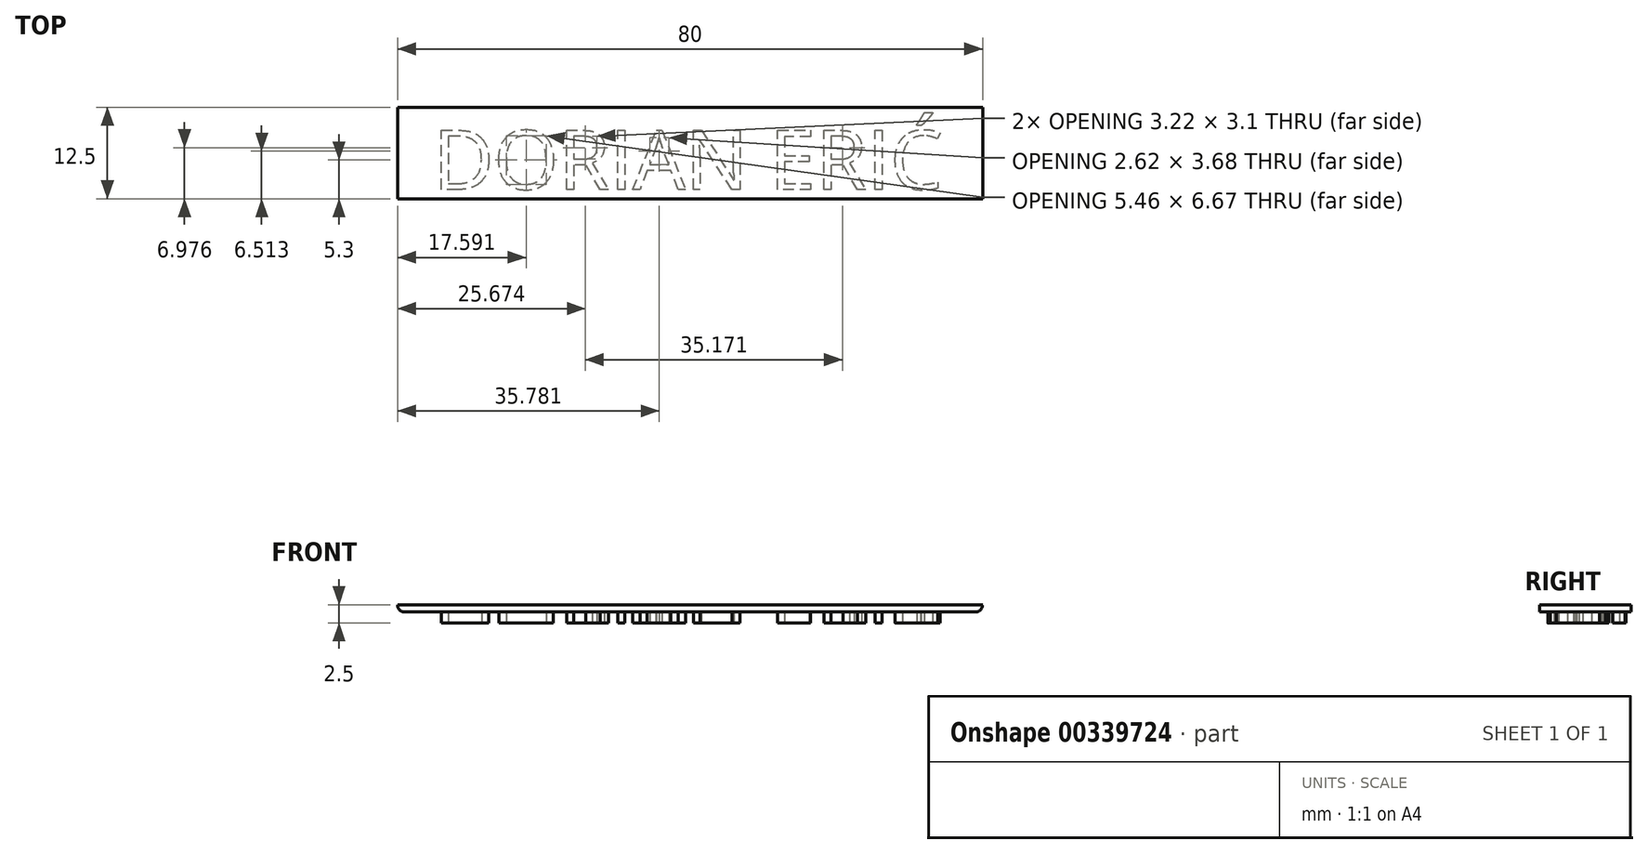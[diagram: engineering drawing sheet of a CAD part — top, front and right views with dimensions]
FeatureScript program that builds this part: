
annotation { "Feature Type Name" : "Feature", "Feature Type Description" : "" }
export const myFeature = defineFeature(function(context is Context, id is Id, definition is map)
    precondition{}
    {
        {
            var Q0;
            Q0=qCreatedBy(makeId("Top.planeOp"),FACE);
            var sketch = newSketch(context, id + "F0", { "sketchPlane" : qUnion([Q0])});
            skLineSegment(sketch, "E0.bottom", {"start": v(40, 6.25) * mm, "end": v(-40, 6.25) * mm});
            skLineSegment(sketch, "E0.top", {"start": v(40, -6.25) * mm, "end": v(-40, -6.25) * mm});
            skLineSegment(sketch, "E0.left", {"start": v(40, 6.25) * mm, "end": v(40, -6.25) * mm});
            skLineSegment(sketch, "E0.right", {"start": v(-40, 6.25) * mm, "end": v(-40, -6.25) * mm});
            skPoint(sketch, "E0.middle", {"position": v(0, 0) * mm});
            skText(sketch, "E1", { "text": "DORIAN ERIĆ", "fontName": "OpenSans-Regular.ttf"});
            const initialGuessF0  = {"E1": [-0.0351, -0.005, 1, 0, 0.00817]};
            skSetInitialGuess(sketch, initialGuessF0);
            skSolve(sketch);
        }
        {
            var Q0;
            Q0=makeQuery(id+"F0.imprint","IMPRINT",FACE,{"disambiguationData":[TD([[makeQuery(id+"F0.imprint","IMPRINT",EDGE,{"derivedFrom":sQuery(id+"F0.wireOp",EDGE,"E0.top")}),-1.0]])]});
            var sketch = newSketch(context, id + "F1", { "sketchPlane" : qUnion([Q0])});
            skLineSegment(sketch, "E2.bottom", {"start": v(40, -6.25) * mm, "end": v(-40, -6.25) * mm});
            skLineSegment(sketch, "E2.top", {"start": v(40, 6.25) * mm, "end": v(-40, 6.25) * mm});
            skLineSegment(sketch, "E2.left", {"start": v(40, -6.25) * mm, "end": v(40, 6.25) * mm});
            skLineSegment(sketch, "E2.right", {"start": v(-40, -6.25) * mm, "end": v(-40, 6.25) * mm});
            skPoint(sketch, "E2.middle", {"position": v(0, 0) * mm});
            skSolve(sketch);
        }
        {
            var Q0;
            Q0 = qSketchRegion(id + "F1", true);
            extrude(context, id + "F2", {"entities" : qUnion([Q0]), "depth" : .5 * mm});
        }
        {
            var Q0;
            Q0=makeQuery(id+"F0.imprint","IMPRINT",FACE,{"disambiguationData":[TD([[makeQuery(id+"F0.imprint","IMPRINT",EDGE,{"derivedFrom":sQuery(id+"F0.wireOp",EDGE,"E1.sketch_text.stroke-103")}),1.0]])]});
            var Q1;
            Q1=makeQuery(id+"F0.imprint","IMPRINT",FACE,{"disambiguationData":[TD([[makeQuery(id+"F0.imprint","IMPRINT",EDGE,{"derivedFrom":sQuery(id+"F0.wireOp",EDGE,"E0.bottom")}),1.0]])]});
            var Q2;
            Q2=makeQuery(id+"F0.imprint","IMPRINT",FACE,{"disambiguationData":[TD([[makeQuery(id+"F0.imprint","IMPRINT",EDGE,{"derivedFrom":sQuery(id+"F0.wireOp",EDGE,"E1.sketch_text.stroke-60")}),1.0]])]});
            var Q3;
            Q3=makeQuery(id+"F0.imprint","IMPRINT",FACE,{"disambiguationData":[TD([[makeQuery(id+"F0.imprint","IMPRINT",EDGE,{"derivedFrom":sQuery(id+"F0.wireOp",EDGE,"E1.sketch_text.stroke-41")}),1.0]])]});
            var Q4;
            Q4=makeQuery(id+"F0.imprint","IMPRINT",FACE,{"disambiguationData":[TD([[makeQuery(id+"F0.imprint","IMPRINT",EDGE,{"derivedFrom":sQuery(id+"F0.wireOp",EDGE,"E1.sketch_text.stroke-22")}),1.0]])]});
            var Q5;
            Q5=makeQuery(id+"F0.imprint","IMPRINT",FACE,{"disambiguationData":[TD([[makeQuery(id+"F0.imprint","IMPRINT",EDGE,{"derivedFrom":sQuery(id+"F0.wireOp",EDGE,"E1.sketch_text.stroke-7")}),1.0]])]});
            extrude(context, id + "F3", {"entities" : qUnion([Q0, Q1, Q2, Q3, Q4, Q5]), "operationType" : NewBodyOperationType.REMOVE, "depth" : 1 * mm});
        }
        {
            var Q0;
            Q0=makeQuery(id+"F2.opExtrude","CAP_FACE",FACE,{"disambiguationData":[OSD([sQuery(id+"F1.wireOp",EDGE,"E2.bottom"),sQuery(id+"F1.wireOp",EDGE,"E2.top"),sQuery(id+"F1.wireOp",EDGE,"E2.left"),sQuery(id+"F1.wireOp",EDGE,"E2.right")])],"isStart":true});
            extrude(context, id + "F4", {"entities" : qUnion([Q0]), "operationType" : NewBodyOperationType.ADD, "depth" : 1 * mm});
        }
        {
            var Q0;
            Q0=makeQuery(id+"F3.boolean.opBoolean","SPLIT",FACE,{"disambiguationData":[TD([makeQuery(id+"F3.opExtrude","SWEPT_FACE",FACE,{"disambiguationData":[OSD([sQuery(id+"F0.wireOp",EDGE,"E1.sketch_text.stroke-0")])]})])],"derivedFrom":makeQuery(id+"F2.opExtrude","CAP_FACE",FACE,{"disambiguationData":[OSD([sQuery(id+"F1.wireOp",EDGE,"E2.bottom"),sQuery(id+"F1.wireOp",EDGE,"E2.top"),sQuery(id+"F1.wireOp",EDGE,"E2.left"),sQuery(id+"F1.wireOp",EDGE,"E2.right")])],"isStart":false})});
            var sketch = newSketch(context, id + "F5", { "sketchPlane" : qUnion([Q0])});
            skLineSegment(sketch, "E3.bottom", {"start": v(-40, 6.25) * mm, "end": v(40, 6.25) * mm});
            skLineSegment(sketch, "E3.top", {"start": v(-40, -6.25) * mm, "end": v(40, -6.25) * mm});
            skLineSegment(sketch, "E3.left", {"start": v(-40, 6.25) * mm, "end": v(-40, -6.25) * mm});
            skLineSegment(sketch, "E3.right", {"start": v(40, 6.25) * mm, "end": v(40, -6.25) * mm});
            skPoint(sketch, "E3.middle", {"position": v(0, 0) * mm});
            skSolve(sketch);
        }
        {
            var Q0;
            Q0=makeQuery(id+"F5.imprint","IMPRINT",FACE,{"disambiguationData":[TD([[makeQuery(id+"F5.imprint","IMPRINT",EDGE,{"derivedFrom":sQuery(id+"F5.wireOp",EDGE,"E3.bottom")}),-1.0]])]});
            var Q1;
            {var subQ0=makeQuery(id+"F2.opExtrude","CAP_FACE",FACE,{"disambiguationData":[OSD([sQuery(id+"F1.wireOp",EDGE,"E2.bottom"),sQuery(id+"F1.wireOp",EDGE,"E2.top"),sQuery(id+"F1.wireOp",EDGE,"E2.left"),sQuery(id+"F1.wireOp",EDGE,"E2.right")])],"isStart":false});Q1=makeQuery(id+"F5.imprint","IMPRINT",FACE,{"disambiguationData":[TD([[makeQuery(id+"F5.imprint","IMPRINT",EDGE,{"derivedFrom":makeQuery(id+"F3.boolean.opBoolean","INTERSECT",EDGE,{"derivedFrom":[subQ0,makeQuery(id+"F3.opExtrude","SWEPT_FACE",FACE,{"disambiguationData":[OSD([sQuery(id+"F0.wireOp",EDGE,"E1.sketch_text.stroke-0")])]})]})}),1.0]])]});}
            extrude(context, id + "F6", {"entities" : qUnion([Q0, Q1]), "depth" : .5 * mm});
        }
        {
            var Q0;
            Q0=makeQuery(id+"F6.opExtrude","CAP_FACE",FACE,{"disambiguationData":[OSD([sQuery(id+"F0.wireOp",EDGE,"E1.sketch_text.stroke-7"),sQuery(id+"F0.wireOp",EDGE,"E1.sketch_text.stroke-8"),sQuery(id+"F0.wireOp",EDGE,"E1.sketch_text.stroke-9"),sQuery(id+"F0.wireOp",EDGE,"E1.sketch_text.stroke-10"),sQuery(id+"F0.wireOp",EDGE,"E1.sketch_text.stroke-11"),sQuery(id+"F0.wireOp",EDGE,"E1.sketch_text.stroke-12"),sQuery(id+"F0.wireOp",EDGE,"E1.sketch_text.stroke-13"),sQuery(id+"F1.wireOp",EDGE,"E2.bottom"),sQuery(id+"F1.wireOp",EDGE,"E2.top"),sQuery(id+"F1.wireOp",EDGE,"E2.left"),sQuery(id+"F1.wireOp",EDGE,"E2.right"),sQuery(id+"F5.wireOp",EDGE,"E3.bottom"),sQuery(id+"F5.wireOp",EDGE,"E3.top"),sQuery(id+"F5.wireOp",EDGE,"E3.left"),sQuery(id+"F5.wireOp",EDGE,"E3.right")])],"isStart":false});
            var sketch = newSketch(context, id + "F7", { "sketchPlane" : qUnion([Q0])});
            skLineSegment(sketch, "E4.bottom", {"start": v(40, 6.25) * mm, "end": v(-40, 6.25) * mm});
            skLineSegment(sketch, "E4.top", {"start": v(40, -6.25) * mm, "end": v(-40, -6.25) * mm});
            skLineSegment(sketch, "E4.left", {"start": v(40, 6.25) * mm, "end": v(40, -6.25) * mm});
            skLineSegment(sketch, "E4.right", {"start": v(-40, 6.25) * mm, "end": v(-40, -6.25) * mm});
            skSolve(sketch);
        }
        {
            var Q0;
            Q0 = qSketchRegion(id + "F7", true);
            extrude(context, id + "F8", {"entities" : qUnion([Q0]), "operationType" : NewBodyOperationType.ADD, "depth" : .5 * mm});
        }
        {
            var Q0;
            Q0=makeQuery(id+"F6.opExtrude","CAP_EDGE",EDGE,{"disambiguationData":[OSD([sQuery(id+"F5.wireOp",EDGE,"E3.left")])],"isStart":true});
            var Q1;
            Q1=makeQuery(id+"F6.opExtrude","CAP_EDGE",EDGE,{"disambiguationData":[OSD([sQuery(id+"F5.wireOp",EDGE,"E3.right")])],"isStart":true});
            fillet(context, id + "F9", {"entities" : qUnion([Q0, Q1]), "radius" : 1 * mm, "tangentPropagation" : true, "allowEdgeOverflow" : false});
        }
        {
            var Q0;
            Q0=makeQuery(id+"F8.opExtrude","CAP_FACE",FACE,{"disambiguationData":[OSD([sQuery(id+"F7.wireOp",EDGE,"E4.bottom"),sQuery(id+"F7.wireOp",EDGE,"E4.top"),sQuery(id+"F7.wireOp",EDGE,"E4.left"),sQuery(id+"F7.wireOp",EDGE,"E4.right")])],"isStart":true});
            extrude(context, id + "F10", {"entities" : qUnion([Q0]), "operationType" : NewBodyOperationType.ADD, "depth" : .5 * mm});
        }
    });
